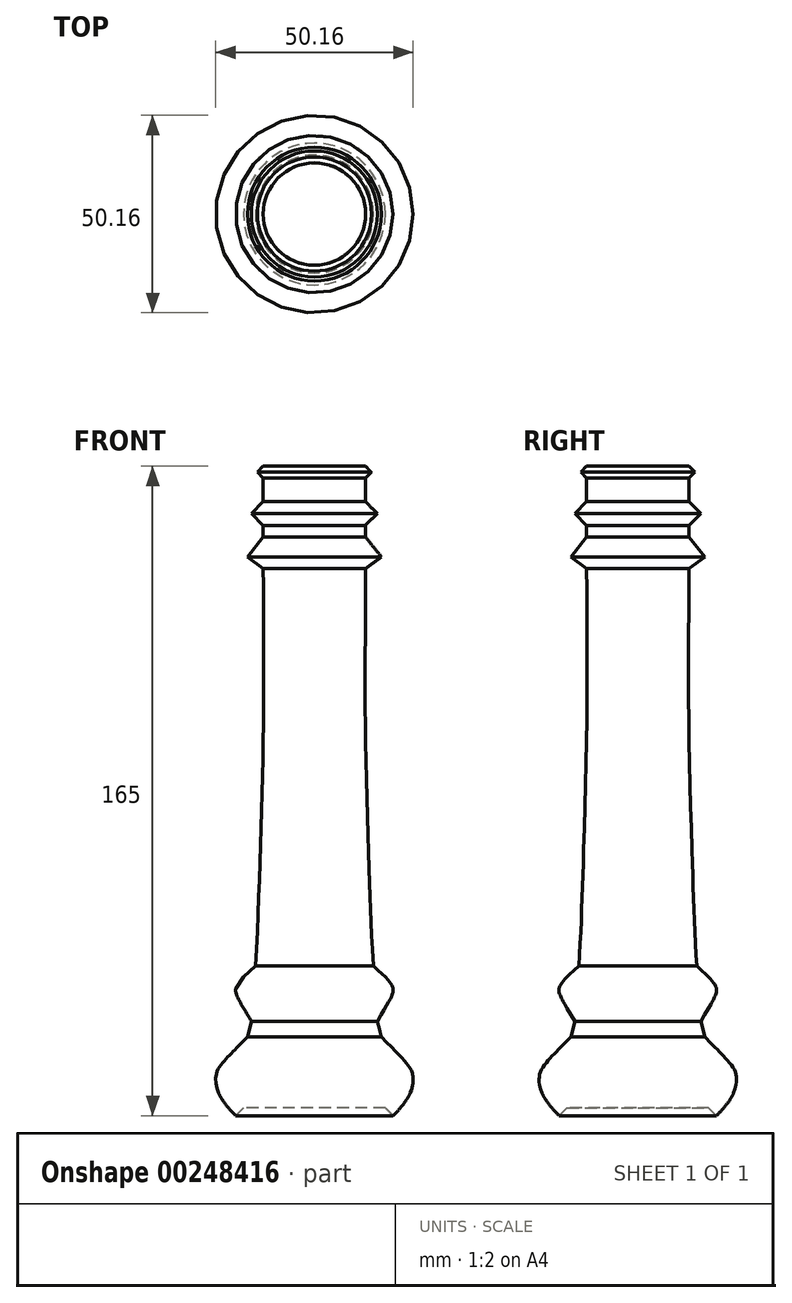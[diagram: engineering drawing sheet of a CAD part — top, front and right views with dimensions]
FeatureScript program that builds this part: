
annotation { "Feature Type Name" : "Feature", "Feature Type Description" : "" }
export const myFeature = defineFeature(function(context is Context, id is Id, definition is map)
    precondition{}
    {
        {
            var Q0;
            Q0=qCreatedBy(makeId("Front.planeOp"),FACE);
            var sketch = newSketch(context, id + "F0", { "sketchPlane" : qUnion([Q0])});
            skLineSegment(sketch, "E0", {"start": v(0, 0) * mm, "end": v(-25, 0) * mm});
            skLineSegment(sketch, "E1", {"start": v(-25, 0) * mm, "end": v(-25, 4) * mm});
            skLineSegment(sketch, "E2", {"start": v(-25, 4) * mm, "end": v(-35, 4) * mm});
            skLineSegment(sketch, "E3", {"start": v(-35, 4) * mm, "end": v(-35, 0) * mm});
            skLineSegment(sketch, "E4", {"start": v(-35, 0) * mm, "end": v(-43, -8) * mm});
            skLineSegment(sketch, "E5", {"start": v(-43, -8) * mm, "end": v(-51, 0) * mm});
            skLineSegment(sketch, "E6", {"start": v(-51, 0) * mm, "end": v(-51, 30) * mm});
            skLineSegment(sketch, "E7", {"start": v(-51, 0) * mm, "end": v(-35, 0) * mm, "construction": true});
            skLineSegment(sketch, "E8", {"start": v(-43, 0) * mm, "end": v(-43, -8) * mm, "construction": true});
            skLineSegment(sketch, "E9", {"start": v(0, 122.85) * mm, "end": v(0, -312.15) * mm});
            skLineSegment(sketch, "E10", {"start": v(-51, 30) * mm, "end": v(51, 30) * mm, "construction": true});
            skLineSegment(sketch, "E11.MirrorCS", {"start": v(51, 0) * mm, "end": v(51, 30) * mm});
            skLineSegment(sketch, "E12.MirrorCS", {"start": v(43, -8) * mm, "end": v(51, 0) * mm});
            skLineSegment(sketch, "E13.MirrorCS", {"start": v(43, 0) * mm, "end": v(43, -8) * mm, "construction": true});
            skLineSegment(sketch, "E14.MirrorCS", {"start": v(51, 0) * mm, "end": v(35, 0) * mm, "construction": true});
            skLineSegment(sketch, "E15.MirrorCS", {"start": v(35, 0) * mm, "end": v(43, -8) * mm});
            skLineSegment(sketch, "E16.MirrorCS", {"start": v(35, 4) * mm, "end": v(35, 0) * mm});
            skLineSegment(sketch, "E17.MirrorCS", {"start": v(25, 4) * mm, "end": v(35, 4) * mm});
            skLineSegment(sketch, "E18.MirrorCS", {"start": v(25, 0) * mm, "end": v(25, 4) * mm});
            skLineSegment(sketch, "E19.MirrorCS", {"start": v(0, 0) * mm, "end": v(25, 0) * mm});
            skLineSegment(sketch, "E20.MirrorCS", {"start": v(-51, 60) * mm, "end": v(-51, 30) * mm});
            skLineSegment(sketch, "E21.MirrorCS", {"start": v(-43, 68) * mm, "end": v(-51, 60) * mm});
            skLineSegment(sketch, "E22.MirrorCS", {"start": v(-51, 60) * mm, "end": v(-35, 60) * mm, "construction": true});
            skLineSegment(sketch, "E23.MirrorCS", {"start": v(-43, 60) * mm, "end": v(-43, 68) * mm, "construction": true});
            skLineSegment(sketch, "E24.MirrorCS", {"start": v(-35, 60) * mm, "end": v(-43, 68) * mm});
            skLineSegment(sketch, "E25.MirrorCS", {"start": v(-35, 56) * mm, "end": v(-35, 60) * mm});
            skLineSegment(sketch, "E26.MirrorCS", {"start": v(-25, 56) * mm, "end": v(-35, 56) * mm});
            skLineSegment(sketch, "E27.MirrorCS", {"start": v(-25, 60) * mm, "end": v(-25, 56) * mm});
            skLineSegment(sketch, "E28.MirrorCS", {"start": v(0, 60) * mm, "end": v(-25, 60) * mm});
            skLineSegment(sketch, "E29.MirrorCS", {"start": v(0, 60) * mm, "end": v(25, 60) * mm});
            skLineSegment(sketch, "E30.MirrorCS", {"start": v(25, 60) * mm, "end": v(25, 56) * mm});
            skLineSegment(sketch, "E31.MirrorCS", {"start": v(25, 56) * mm, "end": v(35, 56) * mm});
            skLineSegment(sketch, "E32.MirrorCS", {"start": v(35, 56) * mm, "end": v(35, 60) * mm});
            skLineSegment(sketch, "E33.MirrorCS", {"start": v(51, 60) * mm, "end": v(35, 60) * mm, "construction": true});
            skLineSegment(sketch, "E34.MirrorCS", {"start": v(35, 60) * mm, "end": v(43, 68) * mm});
            skLineSegment(sketch, "E35.MirrorCS", {"start": v(43, 60) * mm, "end": v(43, 68) * mm, "construction": true});
            skLineSegment(sketch, "E36.MirrorCS", {"start": v(43, 68) * mm, "end": v(51, 60) * mm});
            skLineSegment(sketch, "E37.MirrorCS", {"start": v(51, 60) * mm, "end": v(51, 30) * mm});
            skLineSegment(sketch, "E38", {"start": v(-13, -15) * mm, "end": v(0, -15) * mm});
            skLineSegment(sketch, "E39", {"start": v(0, -180) * mm, "end": v(-20, -180) * mm, "construction": true});
            skLineSegment(sketch, "E40", {"start": v(0, -160) * mm, "end": v(-17, -160) * mm});
            skLineSegment(sketch, "E41", {"start": v(0, -148) * mm, "end": v(-20, -148) * mm, "construction": true});
            skLineSegment(sketch, "E42", {"start": v(0, -27) * mm, "end": v(-16, -27) * mm, "construction": true});
            skFitSpline(sketch, "E43", {"points": [v(-18, 0) * mm, v(-13, -15) * mm], "startDerivative": vector(0, -15.37) * mm, "endDerivative": vector(4.42, -3) * mm});
            skLineSegment(sketch, "E44", {"start": v(-13, -24) * mm, "end": v(-16, -27) * mm});
            skLineSegment(sketch, "E45", {"start": v(-13, -30) * mm, "end": v(-16, -27) * mm});
            skLineSegment(sketch, "E46", {"start": v(-17, -38) * mm, "end": v(-13, -33) * mm});
            skLineSegment(sketch, "E47", {"start": v(-13, -41) * mm, "end": v(-17, -38) * mm});
            skLineSegment(sketch, "E48", {"start": v(-13, -24) * mm, "end": v(0, -24) * mm});
            skLineSegment(sketch, "E49", {"start": v(-25, -170) * mm, "end": v(0, -170) * mm, "construction": true});
            skLineSegment(sketch, "E50", {"start": v(-13, -15) * mm, "end": v(-14.5, -16.5) * mm});
            skLineSegment(sketch, "E51", {"start": v(-14.5, -16.5) * mm, "end": v(-13, -18) * mm});
            skLineSegment(sketch, "E52", {"start": v(-13, -18) * mm, "end": v(-13, -24) * mm});
            skLineSegment(sketch, "E53", {"start": v(-13, -18) * mm, "end": v(0, -18) * mm});
            skLineSegment(sketch, "E54", {"start": v(-14.5, -16.5) * mm, "end": v(0, -16.5) * mm, "construction": true});
            skLineSegment(sketch, "E55", {"start": v(-13, -33) * mm, "end": v(0, -33) * mm});
            skLineSegment(sketch, "E56", {"start": v(-13, -15) * mm, "end": v(-13, -16.5) * mm, "construction": true});
            skLineSegment(sketch, "E57", {"start": v(-13, -16.5) * mm, "end": v(-13, -18) * mm, "construction": true});
            skLineSegment(sketch, "E58", {"start": v(-13, -24) * mm, "end": v(-13, -27) * mm, "construction": true});
            skLineSegment(sketch, "E59", {"start": v(-13, -30) * mm, "end": v(-13, -27) * mm, "construction": true});
            skLineSegment(sketch, "E60", {"start": v(-13, -30) * mm, "end": v(0, -30) * mm});
            skLineSegment(sketch, "E61", {"start": v(-20, -180) * mm, "end": v(-18, -178) * mm});
            skLineSegment(sketch, "E62", {"start": v(-13, -30) * mm, "end": v(-13, -33) * mm});
            skLineSegment(sketch, "E63", {"start": v(-17, -38) * mm, "end": v(0, -38) * mm, "construction": true});
            skLineSegment(sketch, "E64", {"start": v(-13, -41) * mm, "end": v(0, -41) * mm});
            skLineSegment(sketch, "E65", {"start": v(-18, -178) * mm, "end": v(0, -178) * mm});
            skLineSegment(sketch, "E66", {"start": v(-17, -160) * mm, "end": v(-16, -156) * mm});
            skLineSegment(sketch, "E67", {"start": v(-16, -156) * mm, "end": v(0, -156) * mm});
            skLineSegment(sketch, "E68", {"start": v(0, -142) * mm, "end": v(-15, -142) * mm});
            skFitSpline(sketch, "E69", {"points": [v(-16, -156) * mm, v(-20, -148) * mm, v(-15, -142) * mm], "startDerivative": vector(-23.69, 38.43) * mm, "endDerivative": vector(30.52, 26.38) * mm});
            skFitSpline(sketch, "E70", {"points": [v(-17, -160) * mm, v(-25, -170) * mm, v(-20, -180) * mm], "startDerivative": vector(-42.36, -42.36) * mm, "endDerivative": vector(32.92, -32.92) * mm});
            skFitSpline(sketch, "E71", {"points": [v(-13, -41) * mm, v(-13, -84) * mm, v(-14, -120) * mm, v(-15, -142) * mm], "startDerivative": vector(0.46, -153.56) * mm, "endDerivative": vector(-6.84, -103.17) * mm});
            skLineSegment(sketch, "E72", {"start": v(-14, -120) * mm, "end": v(0, -120) * mm, "construction": true});
            skLineSegment(sketch, "E73", {"start": v(-13, -84) * mm, "end": v(0, -84) * mm, "construction": true});
            skLineSegment(sketch, "E74", {"start": v(-23.36, -176) * mm, "end": v(-21.7, -174.9) * mm});
            skLineSegment(sketch, "E75", {"start": v(-21.7, -174.9) * mm, "end": v(-22.8, -173.23) * mm});
            skLineSegment(sketch, "E76", {"start": v(-22.8, -173.23) * mm, "end": v(-24.34, -174.25) * mm});
            skSolve(sketch);
        }
        {
            var Q0;
            {var subQ1=sQuery(id+"F0.wireOp",EDGE,"E40");Q0=makeQuery(id+"F0.imprint","IMPRINT",FACE,{"disambiguationData":[TD([[makeQuery(id+"F0.imprint","IMPRINT",EDGE,{"derivedFrom":subQ1}),1.0]])]});}
            var Q1;
            {var subQ0=sQuery(id+"F0.wireOp",EDGE,"E67");Q1=makeQuery(id+"F0.imprint","IMPRINT",FACE,{"disambiguationData":[TD([[makeQuery(id+"F0.imprint","IMPRINT",EDGE,{"derivedFrom":subQ0}),1.0]])]});}
            var Q2;
            Q2=makeQuery(id+"F0.imprint","IMPRINT",FACE,{"disambiguationData":[TD([[makeQuery(id+"F0.imprint","IMPRINT",EDGE,{"derivedFrom":sQuery(id+"F0.wireOp",EDGE,"E46")}),-1.0]])]});
            var Q3;
            Q3=makeQuery(id+"F0.imprint","IMPRINT",FACE,{"disambiguationData":[TD([[makeQuery(id+"F0.imprint","IMPRINT",EDGE,{"derivedFrom":sQuery(id+"F0.wireOp",EDGE,"E44")}),1.0]])]});
            var Q4;
            {var subQ0=sQuery(id+"F0.wireOp",EDGE,"E38");Q4=makeQuery(id+"F0.imprint","IMPRINT",FACE,{"disambiguationData":[TD([[makeQuery(id+"F0.imprint","IMPRINT",EDGE,{"derivedFrom":subQ0}),-1.0]])]});}
            var Q5;
            {var subQ0=sQuery(id+"F0.wireOp",EDGE,"E74");Q5=makeQuery(id+"F0.imprint","IMPRINT",FACE,{"disambiguationData":[TD([[makeQuery(id+"F0.imprint","IMPRINT",EDGE,{"derivedFrom":subQ0}),1.0]])]});}
            var Q6;
            Q6=sQuery(id+"F0.wireOp",EDGE,"E9");
            revolve(context, id + "F1", {"entities" : qUnion([Q0, Q1, Q2, Q3, Q4, Q5]), "axis" : qUnion([Q6]), "revolveType" : RevolveType.FULL});
        }
        {
            var Q0;
            {var subQ0=sQuery(id+"F0.wireOp",EDGE,"E48");Q0=makeQuery(id+"F0.imprint","IMPRINT",FACE,{"disambiguationData":[TD([[makeQuery(id+"F0.imprint","IMPRINT",EDGE,{"derivedFrom":subQ0}),1.0]])]});}
            var Q1;
            {var subQ0=sQuery(id+"F0.wireOp",EDGE,"E55");Q1=makeQuery(id+"F0.imprint","IMPRINT",FACE,{"disambiguationData":[TD([[makeQuery(id+"F0.imprint","IMPRINT",EDGE,{"derivedFrom":subQ0}),1.0]])]});}
            var Q2;
            {var subQ0=sQuery(id+"F0.wireOp",EDGE,"E40");Q2=makeQuery(id+"F0.imprint","IMPRINT",FACE,{"disambiguationData":[TD([[makeQuery(id+"F0.imprint","IMPRINT",EDGE,{"derivedFrom":subQ0}),-1.0]])]});}
            var Q3;
            Q3=sQuery(id+"F0.wireOp",EDGE,"E9");
            revolve(context, id + "F2", {"entities" : qUnion([Q0, Q1, Q2]), "axis" : qUnion([Q3]), "revolveType" : RevolveType.FULL});
        }
        {
            var Q0;
            {var subQ0=sQuery(id+"F0.wireOp",EDGE,"E64");Q0=makeQuery(id+"F0.imprint","IMPRINT",FACE,{"disambiguationData":[TD([[makeQuery(id+"F0.imprint","IMPRINT",EDGE,{"derivedFrom":subQ0}),-1.0]])]});}
            var Q1;
            Q1=sQuery(id+"F0.wireOp",EDGE,"E9");
            revolve(context, id + "F3", {"entities" : qUnion([Q0]), "axis" : qUnion([Q1]), "revolveType" : RevolveType.FULL});
        }
    });
